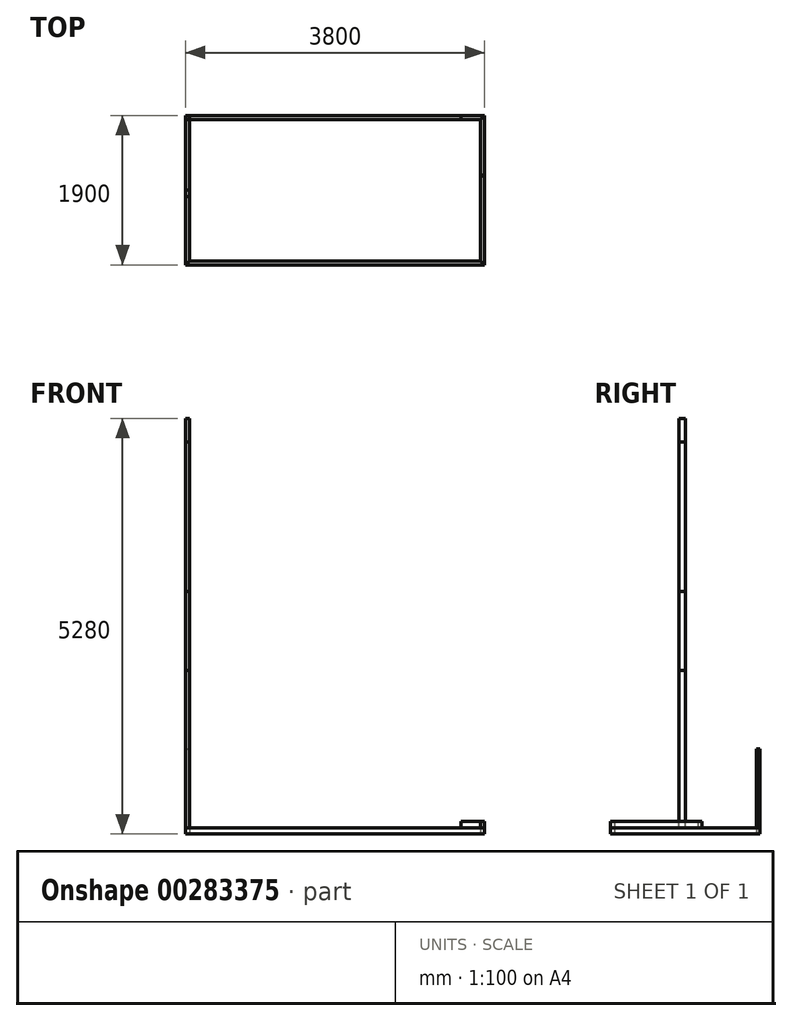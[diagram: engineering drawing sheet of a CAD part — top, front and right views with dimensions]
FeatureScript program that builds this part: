
annotation { "Feature Type Name" : "Feature", "Feature Type Description" : "" }
export const myFeature = defineFeature(function(context is Context, id is Id, definition is map)
    precondition{}
    {
        {
            var Q0;
            Q0=qCreatedBy(makeId("Top.planeOp"),FACE);
            var sketch = newSketch(context, id + "F0", { "sketchPlane" : qUnion([Q0])});
            skLineSegment(sketch, "E0.bottom", {"start": v(1900, 950) * mm, "end": v(-1900, 950) * mm});
            skLineSegment(sketch, "E0.top", {"start": v(1900, -950) * mm, "end": v(-1900, -950) * mm});
            skLineSegment(sketch, "E0.left", {"start": v(1900, 950) * mm, "end": v(1900, -950) * mm});
            skLineSegment(sketch, "E0.right", {"start": v(-1900, 950) * mm, "end": v(-1900, -950) * mm});
            skPoint(sketch, "E0.middle", {"position": v(0, 0) * mm});
            skLineSegment(sketch, "E1.0", {"start": v(1850, 900) * mm, "end": v(-1850, 900) * mm});
            skLineSegment(sketch, "E1.1", {"start": v(1850, 900) * mm, "end": v(1850, -900) * mm});
            skLineSegment(sketch, "E1.2", {"start": v(1850, -900) * mm, "end": v(-1850, -900) * mm});
            skLineSegment(sketch, "E1.3", {"start": v(-1850, 900) * mm, "end": v(-1850, -900) * mm});
            skLineSegment(sketch, "E2", {"start": v(-1850, 900) * mm, "end": v(-1900, 950) * mm});
            skLineSegment(sketch, "E3", {"start": v(1850, 900) * mm, "end": v(1900, 950) * mm});
            skLineSegment(sketch, "E4", {"start": v(1900, -950) * mm, "end": v(1850, -900) * mm});
            skLineSegment(sketch, "E5", {"start": v(-1900, -950) * mm, "end": v(-1850, -900) * mm});
            skSolve(sketch);
        }
        {
            var Q0;
            Q0=makeQuery(id+"F0.imprint","IMPRINT",FACE,{"disambiguationData":[TD([[makeQuery(id+"F0.imprint","IMPRINT",EDGE,{"derivedFrom":sQuery(id+"F0.wireOp",EDGE,"E0.bottom")}),1.0]])]});
            extrude(context, id + "F1", {"entities" : qUnion([Q0]), "depth" : 80 * mm});
        }
        {
            var Q0;
            Q0=makeQuery(id+"F0.imprint","IMPRINT",FACE,{"disambiguationData":[TD([[makeQuery(id+"F0.imprint","IMPRINT",EDGE,{"derivedFrom":sQuery(id+"F0.wireOp",EDGE,"E0.right")}),1.0]])]});
            extrude(context, id + "F2", {"entities" : qUnion([Q0]), "depth" : 80 * mm});
        }
        {
            var Q0;
            Q0=makeQuery(id+"F0.imprint","IMPRINT",FACE,{"disambiguationData":[TD([[makeQuery(id+"F0.imprint","IMPRINT",EDGE,{"derivedFrom":sQuery(id+"F0.wireOp",EDGE,"E0.top")}),-1.0]])]});
            extrude(context, id + "F3", {"entities" : qUnion([Q0]), "depth" : 80 * mm});
        }
        {
            var Q0;
            Q0=makeQuery(id+"F0.imprint","IMPRINT",FACE,{"disambiguationData":[TD([[makeQuery(id+"F0.imprint","IMPRINT",EDGE,{"derivedFrom":sQuery(id+"F0.wireOp",EDGE,"E0.left")}),-1.0]])]});
            extrude(context, id + "F4", {"entities" : qUnion([Q0]), "depth" : 80 * mm});
        }
        {
            var Q0;
            Q0=qCreatedBy(makeId("Front.planeOp"),FACE);
            var sketch = newSketch(context, id + "F5", { "sketchPlane" : qUnion([Q0])});
            skPoint(sketch, "E6.0", {"position": v(-1900, 80) * mm});
            skLineSegment(sketch, "E7.bottom", {"start": v(-1900, 80) * mm, "end": v(-1850, 80) * mm});
            skLineSegment(sketch, "E7.top", {"start": v(-1900, 2080) * mm, "end": v(-1850, 2080) * mm});
            skLineSegment(sketch, "E7.left", {"start": v(-1900, 80) * mm, "end": v(-1900, 2080) * mm});
            skLineSegment(sketch, "E7.right", {"start": v(-1850, 80) * mm, "end": v(-1850, 2080) * mm});
            skSolve(sketch);
        }
        {
            var Q0;
            Q0=makeQuery(id+"F5.imprint","IMPRINT",FACE,{"disambiguationData":[TD([[makeQuery(id+"F5.imprint","IMPRINT",EDGE,{"derivedFrom":sQuery(id+"F5.wireOp",EDGE,"E7.bottom")}),1.0]])]});
            extrude(context, id + "F6", {"entities" : qUnion([Q0]), "depth" : 80 * mm});
        }
        {
            var Q0;
            Q0=makeQuery(id+"F1.opExtrude","CAP_FACE",FACE,{"disambiguationData":[OSD([sQuery(id+"F0.wireOp",EDGE,"E0.bottom"),sQuery(id+"F0.wireOp",EDGE,"E1.0"),sQuery(id+"F0.wireOp",EDGE,"E2"),sQuery(id+"F0.wireOp",EDGE,"E3")])],"isStart":false});
            var sketch = newSketch(context, id + "F7", { "sketchPlane" : qUnion([Q0])});
            skPoint(sketch, "E8.0", {"position": v(-1900, 950) * mm});
            skPoint(sketch, "E8.1", {"position": v(-1850, 900) * mm});
            skLineSegment(sketch, "E9.bottom", {"start": v(-1900, 950) * mm, "end": v(-1850, 950) * mm});
            skLineSegment(sketch, "E9.top", {"start": v(-1900, 900) * mm, "end": v(-1850, 900) * mm});
            skLineSegment(sketch, "E9.left", {"start": v(-1900, 950) * mm, "end": v(-1900, 900) * mm});
            skLineSegment(sketch, "E9.right", {"start": v(-1850, 950) * mm, "end": v(-1850, 900) * mm});
            skSolve(sketch);
        }
        {
            var Q0;
            Q0 = qSketchRegion(id + "F7", true);
            extrude(context, id + "F8", {"entities" : qUnion([Q0]), "depth" : 1000 * mm});
        }
        {
            var Q0;
            Q0=makeQuery(id+"F6.opExtrude","SWEPT_FACE",FACE,{"disambiguationData":[OSD([sQuery(id+"F5.wireOp",EDGE,"E7.top")])]});
            extrude(context, id + "F9", {"entities" : qUnion([Q0]), "depth" : 1000 * mm});
        }
        {
            var Q0;
            Q0=makeQuery(id+"F9.opExtrude","CAP_FACE",FACE,{"disambiguationData":[OSD([sQuery(id+"F5.wireOp",EDGE,"E7.top")])],"isStart":false});
            extrude(context, id + "F10", {"entities" : qUnion([Q0]), "depth" : 1900 * mm});
        }
        {
            var Q0;
            Q0=makeQuery(id+"F10.opExtrude","CAP_FACE",FACE,{"disambiguationData":[OSD([sQuery(id+"F5.wireOp",EDGE,"E7.top")])],"isStart":false});
            extrude(context, id + "F11", {"entities" : qUnion([Q0]), "depth" : 300 * mm});
        }
        {
            var Q0;
            Q0=makeQuery(id+"F1.opExtrude","CAP_FACE",FACE,{"disambiguationData":[OSD([sQuery(id+"F0.wireOp",EDGE,"E0.bottom"),sQuery(id+"F0.wireOp",EDGE,"E1.0"),sQuery(id+"F0.wireOp",EDGE,"E2"),sQuery(id+"F0.wireOp",EDGE,"E3")])],"isStart":false});
            var sketch = newSketch(context, id + "F12", { "sketchPlane" : qUnion([Q0])});
            skLineSegment(sketch, "E10", {"start": v(1850, 900) * mm, "end": v(1900, 950) * mm});
            skLineSegment(sketch, "E11", {"start": v(1900, 950) * mm, "end": v(1600, 950) * mm});
            skLineSegment(sketch, "E12", {"start": v(1600, 950) * mm, "end": v(1600, 900) * mm});
            skLineSegment(sketch, "E13", {"start": v(1600, 900) * mm, "end": v(1850, 900) * mm});
            skSolve(sketch);
        }
        {
            var Q0;
            Q0 = qSketchRegion(id + "F12", true);
            extrude(context, id + "F13", {"entities" : qUnion([Q0]), "depth" : 80 * mm});
        }
        {
            var Q0;
            Q0=makeQuery(id+"F4.opExtrude","CAP_FACE",FACE,{"disambiguationData":[OSD([sQuery(id+"F0.wireOp",EDGE,"E0.left"),sQuery(id+"F0.wireOp",EDGE,"E1.1"),sQuery(id+"F0.wireOp",EDGE,"E3"),sQuery(id+"F0.wireOp",EDGE,"E4")])],"isStart":false});
            var sketch = newSketch(context, id + "F14", { "sketchPlane" : qUnion([Q0])});
            skLineSegment(sketch, "E14.0", {"start": v(1900, -950) * mm, "end": v(1850, -900) * mm});
            skLineSegment(sketch, "E15", {"start": v(1850, -900) * mm, "end": v(1850, 160) * mm});
            skLineSegment(sketch, "E16", {"start": v(1850, 160) * mm, "end": v(1900, 210) * mm});
            skLineSegment(sketch, "E17", {"start": v(1900, 210) * mm, "end": v(1900, -950) * mm});
            skSolve(sketch);
        }
        {
            var Q0;
            Q0 = qSketchRegion(id + "F14", true);
            extrude(context, id + "F15", {"entities" : qUnion([Q0]), "depth" : 80 * mm});
        }
    });
